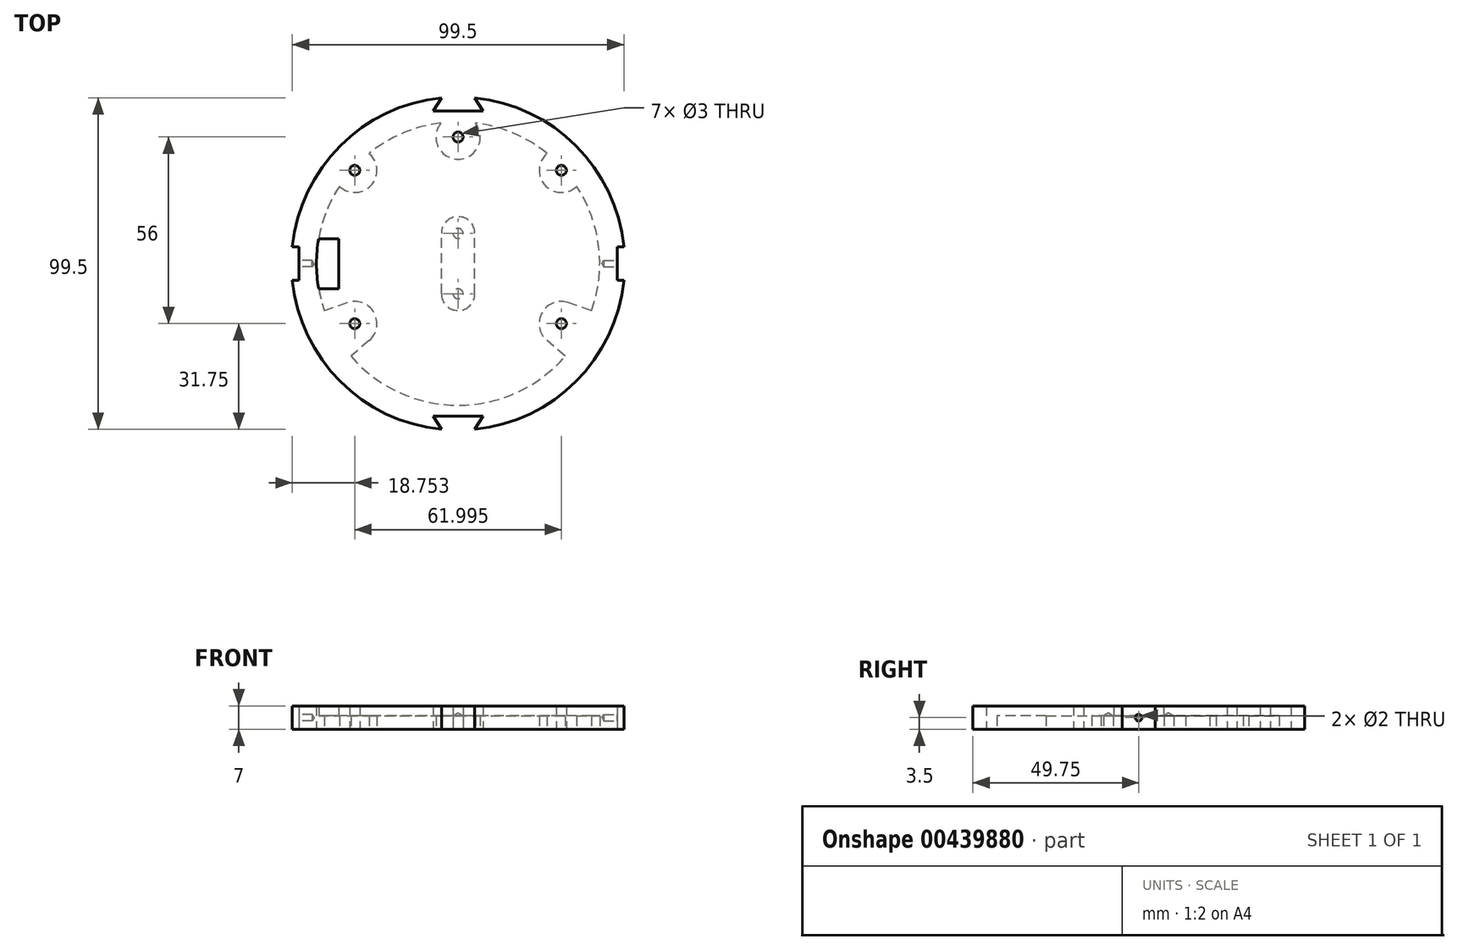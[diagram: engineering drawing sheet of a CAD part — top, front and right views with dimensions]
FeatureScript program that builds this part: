
annotation { "Feature Type Name" : "Feature", "Feature Type Description" : "" }
export const myFeature = defineFeature(function(context is Context, id is Id, definition is map)
    precondition{}
    {
        {
            var Q0;
            Q0=qCreatedBy(makeId("Top.planeOp"),FACE);
            var sketch = newSketch(context, id + "F0", { "sketchPlane" : qUnion([Q0])});
            skLineSegment(sketch, "E0", {"start": v(-49.75, 5) * mm, "end": v(-47.75, 5) * mm});
            skLineSegment(sketch, "E1.0.1.0", {"start": v(-49.75, -5) * mm, "end": v(-47.75, -5) * mm});
            skLineSegment(sketch, "E2.right", {"start": v(-47.75, 5) * mm, "end": v(-47.75, -5) * mm});
            skLineSegment(sketch, "E3.bottom", {"start": v(49.75, 5) * mm, "end": v(47.75, 5) * mm});
            skLineSegment(sketch, "E3.top", {"start": v(49.75, -5) * mm, "end": v(47.75, -5) * mm});
            skLineSegment(sketch, "E3.right", {"start": v(47.75, 5) * mm, "end": v(47.75, -5) * mm});
            skLineSegment(sketch, "E4.trimOffspring", {"start": v(47.75, 5) * mm, "end": v(49.75, 5) * mm});
            skLineSegment(sketch, "E5.trimOffspring", {"start": v(47.75, -5) * mm, "end": v(49.75, -5) * mm});
            skArc(sketch, "E6", {"start": v(-5, 49.75) * mm, "mid": v(-35.36, 35.36) * mm, "end": v(-49.75, 5) * mm});
            skArc(sketch, "E7.trimOffspring", {"start": v(-49.75, -5) * mm, "mid": v(-35.36, -35.36) * mm, "end": v(-5, -49.75) * mm});
            skArc(sketch, "E8.trimOffspring", {"start": v(49.75, 5) * mm, "mid": v(35.36, 35.36) * mm, "end": v(5, 49.75) * mm});
            skArc(sketch, "E9.trimOffspring", {"start": v(5, -49.75) * mm, "mid": v(35.36, -35.36) * mm, "end": v(49.75, -5) * mm});
            skCircle(sketch, "E10", {"center": v(-31, 28) * mm, "radius": 1.5 * mm});
            skCircle(sketch, "E11", {"center": v(0, 38) * mm, "radius": 1.5 * mm});
            skCircle(sketch, "E12", {"center": v(31, 28) * mm, "radius": 1.5 * mm});
            skCircle(sketch, "E13", {"center": v(-31, -18) * mm, "radius": 1.5 * mm});
            skCircle(sketch, "E14", {"center": v(31, -18) * mm, "radius": 1.5 * mm});
            skLineSegment(sketch, "E15", {"start": v(7.5, 45.75) * mm, "end": v(-7.5, 45.75) * mm});
            skLineSegment(sketch, "E16", {"start": v(-7.5, -45.75) * mm, "end": v(7.5, -45.75) * mm});
            skLineSegment(sketch, "E17", {"start": v(-5, 49.75) * mm, "end": v(-7.5, 45.75) * mm});
            skLineSegment(sketch, "E18", {"start": v(5, 49.75) * mm, "end": v(7.5, 45.75) * mm});
            skLineSegment(sketch, "E19", {"start": v(-7.5, -45.75) * mm, "end": v(-5, -49.75) * mm});
            skLineSegment(sketch, "E20", {"start": v(5, -49.75) * mm, "end": v(7.5, -45.75) * mm});
            skCircle(sketch, "E21", {"center": v(0, 0) * mm, "radius": 42.5 * mm, "construction": true});
            skLineSegment(sketch, "E22.bottom", {"start": v(-41.83, 7.5) * mm, "end": v(-35.83, 7.5) * mm});
            skLineSegment(sketch, "E22.top", {"start": v(-41.83, -7.5) * mm, "end": v(-35.83, -7.5) * mm});
            skLineSegment(sketch, "E22.left", {"start": v(-41.83, 7.5) * mm, "end": v(-41.83, -7.5) * mm});
            skLineSegment(sketch, "E22.right", {"start": v(-35.83, 7.5) * mm, "end": v(-35.83, -7.5) * mm});
            skArc(sketch, "E23", {"start": v(-41.83, 7.5) * mm, "mid": v(-42.5, 0) * mm, "end": v(-41.83, -7.5) * mm});
            skSolve(sketch);
        }
        {
            var Q0;
            Q0 = qSketchRegion(id + "F0", true);
            extrude(context, id + "F1", {"entities" : qUnion([Q0]), "offsetDistance" : 25 * mm, "depth" : 7 * mm});
        }
        {
            var Q0;
            Q0=makeQuery(id+"F1.opExtrude","CAP_FACE",FACE,{"disambiguationData":[OSD([sQuery(id+"F0.wireOp",EDGE,"E0"),sQuery(id+"F0.wireOp",EDGE,"E1.0.1.0"),sQuery(id+"F0.wireOp",EDGE,"E2.right"),sQuery(id+"F0.wireOp",EDGE,"E3.right"),sQuery(id+"F0.wireOp",EDGE,"6F78V14t-ZdTv-VjlB-1T6a-OLiU7aMDUZpK.top"),sQuery(id+"F0.wireOp",EDGE,"6F78V14t-ZdTv-VjlB-1T6a-OLiU7aMDUZpK.left"),sQuery(id+"F0.wireOp",EDGE,"6F78V14t-ZdTv-VjlB-1T6a-OLiU7aMDUZpK.right"),sQuery(id+"F0.wireOp",EDGE,"PvTYHQWE-3ALD-PmBr-tVXn-1hqZbBmZ8mVZ.top"),sQuery(id+"F0.wireOp",EDGE,"E4.trimOffspring"),sQuery(id+"F0.wireOp",EDGE,"E5.trimOffspring"),sQuery(id+"F0.wireOp",EDGE,"1bcc615c-06b4-494b-89bc-5a61939d49d9.trimOffspring"),sQuery(id+"F0.wireOp",EDGE,"d66e13da-aae6-4b5e-80dc-d0fbbee3e63b.trimOffspring"),sQuery(id+"F0.wireOp",EDGE,"E6"),sQuery(id+"F0.wireOp",EDGE,"E7.trimOffspring"),sQuery(id+"F0.wireOp",EDGE,"E8.trimOffspring"),sQuery(id+"F0.wireOp",EDGE,"E9.trimOffspring"),sQuery(id+"F0.wireOp",EDGE,"E10"),sQuery(id+"F0.wireOp",EDGE,"E11"),sQuery(id+"F0.wireOp",EDGE,"E12"),sQuery(id+"F0.wireOp",EDGE,"E13"),sQuery(id+"F0.wireOp",EDGE,"E14")])],"isStart":true});
            var sketch = newSketch(context, id + "F2", { "sketchPlane" : qUnion([Q0])});
            skArc(sketch, "E24", {"start": v(-40.08, 14.15) * mm, "mid": v(-42.2, -5.05) * mm, "end": v(-35.6, -23.2) * mm});
            skArc(sketch, "E25", {"start": v(-33.21, 11.72) * mm, "mid": v(-25.24, 14.66) * mm, "end": v(-26.64, 23.03) * mm});
            skArc(sketch, "E26", {"start": v(26.64, 23.03) * mm, "mid": v(25.24, 14.66) * mm, "end": v(33.21, 11.72) * mm});
            skArc(sketch, "E27", {"start": v(-26.7, -33.07) * mm, "mid": v(-26.06, -23.54) * mm, "end": v(-35.6, -23.2) * mm});
            skArc(sketch, "E28", {"start": v(35.6, -23.2) * mm, "mid": v(26.06, -23.54) * mm, "end": v(26.7, -33.07) * mm});
            skArc(sketch, "E29", {"start": v(5.18, -42.18) * mm, "mid": v(0, -31.34) * mm, "end": v(-5.18, -42.18) * mm});
            skLineSegment(sketch, "E30", {"start": v(-26.64, 23.03) * mm, "end": v(-32.15, 27.8) * mm});
            skLineSegment(sketch, "E31", {"start": v(-33.21, 11.72) * mm, "end": v(-40.08, 14.15) * mm});
            skLineSegment(sketch, "E32", {"start": v(32.15, 27.8) * mm, "end": v(26.64, 23.03) * mm});
            skLineSegment(sketch, "E33", {"start": v(40.08, 14.15) * mm, "end": v(33.21, 11.72) * mm});
            skArc(sketch, "E34.trimOffspring", {"start": v(32.15, 27.8) * mm, "mid": v(0, 42.5) * mm, "end": v(-32.15, 27.8) * mm});
            skArc(sketch, "E35.trimOffspring", {"start": v(-26.7, -33.07) * mm, "mid": v(-16.57, -39.14) * mm, "end": v(-5.18, -42.18) * mm});
            skArc(sketch, "E36.trimOffspring", {"start": v(35.6, -23.2) * mm, "mid": v(42.2, -5.05) * mm, "end": v(40.08, 14.15) * mm});
            skArc(sketch, "E37.trimOffspring", {"start": v(5.18, -42.18) * mm, "mid": v(16.57, -39.14) * mm, "end": v(26.7, -33.07) * mm});
            skSolve(sketch);
        }
        {
            var Q0;
            Q0 = qSketchRegion(id + "F2", true);
            extrude(context, id + "F3", {"entities" : qUnion([Q0]), "operationType" : NewBodyOperationType.REMOVE, "oppositeDirection" : true, "depth" : 4 * mm});
        }
        {
            var Q0;
            Q0=makeQuery(id+"F1.opExtrude","SWEPT_FACE",FACE,{"disambiguationData":[OSD([sQuery(id+"F0.wireOp",EDGE,"E2.right")])]});
            var sketch = newSketch(context, id + "F4", { "sketchPlane" : qUnion([Q0])});
            skCircle(sketch, "E38", {"center": v(0, 3.5) * mm, "radius": 1.5 * mm});
            skSolve(sketch);
        }
        {
            var Q0;
            Q0=sQuery(id+"F4.wireOp",VERTEX,"E38.center");
            var Q1;
            Q1=makeQuery(id+"F1.opExtrude","SWEPT_BODY",BODY,{"disambiguationData":[OSD([sQuery(id+"F0.wireOp",EDGE,"E0"),sQuery(id+"F0.wireOp",EDGE,"E1.0.1.0"),sQuery(id+"F0.wireOp",EDGE,"E2.right"),sQuery(id+"F0.wireOp",EDGE,"E3.right"),sQuery(id+"F0.wireOp",EDGE,"6F78V14t-ZdTv-VjlB-1T6a-OLiU7aMDUZpK.top"),sQuery(id+"F0.wireOp",EDGE,"6F78V14t-ZdTv-VjlB-1T6a-OLiU7aMDUZpK.left"),sQuery(id+"F0.wireOp",EDGE,"6F78V14t-ZdTv-VjlB-1T6a-OLiU7aMDUZpK.right"),sQuery(id+"F0.wireOp",EDGE,"PvTYHQWE-3ALD-PmBr-tVXn-1hqZbBmZ8mVZ.top"),sQuery(id+"F0.wireOp",EDGE,"E4.trimOffspring"),sQuery(id+"F0.wireOp",EDGE,"E5.trimOffspring"),sQuery(id+"F0.wireOp",EDGE,"1bcc615c-06b4-494b-89bc-5a61939d49d9.trimOffspring"),sQuery(id+"F0.wireOp",EDGE,"d66e13da-aae6-4b5e-80dc-d0fbbee3e63b.trimOffspring"),sQuery(id+"F0.wireOp",EDGE,"E6"),sQuery(id+"F0.wireOp",EDGE,"E7.trimOffspring"),sQuery(id+"F0.wireOp",EDGE,"E8.trimOffspring"),sQuery(id+"F0.wireOp",EDGE,"E9.trimOffspring"),sQuery(id+"F0.wireOp",EDGE,"E10"),sQuery(id+"F0.wireOp",EDGE,"E11"),sQuery(id+"F0.wireOp",EDGE,"E12"),sQuery(id+"F0.wireOp",EDGE,"E13"),sQuery(id+"F0.wireOp",EDGE,"E14")])]});
            hole(context, id + "F5", {"style" : HoleStyle.SIMPLE, "endStyle" : HoleEndStyle.BLIND, "holeDiameter" : 2 * mm, "holeDepth" : 4 * mm, "isTappedThrough" : true, "tappedDepth" : 12 * mm, "tapClearance" : 3, "startFromSketch" : true, "locations" : qUnion([Q0]), "scope" : qUnion([Q1])});
        }
        {
            var Q0;
            Q0=makeQuery(id+"F1.opExtrude","SWEPT_FACE",FACE,{"disambiguationData":[OSD([sQuery(id+"F0.wireOp",EDGE,"E3.right")])]});
            var sketch = newSketch(context, id + "F6", { "sketchPlane" : qUnion([Q0])});
            skCircle(sketch, "E39", {"center": v(0, 3.5) * mm, "radius": 0.95 * mm});
            skSolve(sketch);
        }
        {
            var Q0;
            Q0=sQuery(id+"F6.wireOp",VERTEX,"E39.center");
            var Q1;
            Q1=makeQuery(id+"F1.opExtrude","SWEPT_BODY",BODY,{"disambiguationData":[OSD([sQuery(id+"F0.wireOp",EDGE,"E0"),sQuery(id+"F0.wireOp",EDGE,"E1.0.1.0"),sQuery(id+"F0.wireOp",EDGE,"E2.right"),sQuery(id+"F0.wireOp",EDGE,"E3.right"),sQuery(id+"F0.wireOp",EDGE,"6F78V14t-ZdTv-VjlB-1T6a-OLiU7aMDUZpK.top"),sQuery(id+"F0.wireOp",EDGE,"6F78V14t-ZdTv-VjlB-1T6a-OLiU7aMDUZpK.left"),sQuery(id+"F0.wireOp",EDGE,"6F78V14t-ZdTv-VjlB-1T6a-OLiU7aMDUZpK.right"),sQuery(id+"F0.wireOp",EDGE,"PvTYHQWE-3ALD-PmBr-tVXn-1hqZbBmZ8mVZ.top"),sQuery(id+"F0.wireOp",EDGE,"E4.trimOffspring"),sQuery(id+"F0.wireOp",EDGE,"E5.trimOffspring"),sQuery(id+"F0.wireOp",EDGE,"1bcc615c-06b4-494b-89bc-5a61939d49d9.trimOffspring"),sQuery(id+"F0.wireOp",EDGE,"d66e13da-aae6-4b5e-80dc-d0fbbee3e63b.trimOffspring"),sQuery(id+"F0.wireOp",EDGE,"E6"),sQuery(id+"F0.wireOp",EDGE,"E7.trimOffspring"),sQuery(id+"F0.wireOp",EDGE,"E8.trimOffspring"),sQuery(id+"F0.wireOp",EDGE,"E9.trimOffspring"),sQuery(id+"F0.wireOp",EDGE,"E10"),sQuery(id+"F0.wireOp",EDGE,"E11"),sQuery(id+"F0.wireOp",EDGE,"E12"),sQuery(id+"F0.wireOp",EDGE,"E13"),sQuery(id+"F0.wireOp",EDGE,"E14")])]});
            hole(context, id + "F7", {"style" : HoleStyle.SIMPLE, "endStyle" : HoleEndStyle.BLIND, "holeDiameter" : 2 * mm, "holeDepth" : 4 * mm, "isTappedThrough" : true, "tappedDepth" : 12 * mm, "tapClearance" : 3, "startFromSketch" : true, "locations" : qUnion([Q0]), "scope" : qUnion([Q1])});
        }
        {
            var Q0;
            Q0=qCreatedBy(makeId("Top.planeOp"),FACE);
            var sketch = newSketch(context, id + "F8", { "sketchPlane" : qUnion([Q0])});
            skArc(sketch, "E40", {"start": v(-4.99, -9.06) * mm, "mid": v(0.01, -14.06) * mm, "end": v(5.01, -9.06) * mm});
            skArc(sketch, "E41", {"start": v(5.01, 9.07) * mm, "mid": v(0.01, 14.07) * mm, "end": v(-4.99, 9.07) * mm});
            skLineSegment(sketch, "E42", {"start": v(5.01, -9.06) * mm, "end": v(5.01, 9.07) * mm});
            skLineSegment(sketch, "E43", {"start": v(-4.99, -9.06) * mm, "end": v(-4.99, 9.07) * mm});
            skSolve(sketch);
        }
        {
            var Q0;
            Q0=makeQuery(id+"F8.imprint","IMPRINT",FACE,{"disambiguationData":[TD([[makeQuery(id+"F8.imprint","IMPRINT",EDGE,{"derivedFrom":sQuery(id+"F8.wireOp",EDGE,"E40")}),1.0]])]});
            extrude(context, id + "F9", {"entities" : qUnion([Q0]), "operationType" : NewBodyOperationType.ADD, "depth" : 4 * mm});
        }
        {
            var Q0;
            Q0=sQuery(id+"F8.wireOp",VERTEX,"E40.center");
            var Q1;
            Q1=sQuery(id+"F8.wireOp",VERTEX,"E41.center");
            var Q2;
            Q2=makeQuery(id+"F1.opExtrude","SWEPT_BODY",BODY,{"disambiguationData":[OSD([sQuery(id+"F0.wireOp",EDGE,"E0"),sQuery(id+"F0.wireOp",EDGE,"E1.0.1.0"),sQuery(id+"F0.wireOp",EDGE,"E2.right"),sQuery(id+"F0.wireOp",EDGE,"E3.right"),sQuery(id+"F0.wireOp",EDGE,"E4.trimOffspring"),sQuery(id+"F0.wireOp",EDGE,"E5.trimOffspring"),sQuery(id+"F0.wireOp",EDGE,"E6"),sQuery(id+"F0.wireOp",EDGE,"E7.trimOffspring"),sQuery(id+"F0.wireOp",EDGE,"E8.trimOffspring"),sQuery(id+"F0.wireOp",EDGE,"E9.trimOffspring"),sQuery(id+"F0.wireOp",EDGE,"E10"),sQuery(id+"F0.wireOp",EDGE,"E11"),sQuery(id+"F0.wireOp",EDGE,"E12"),sQuery(id+"F0.wireOp",EDGE,"E13"),sQuery(id+"F0.wireOp",EDGE,"E14"),sQuery(id+"F0.wireOp",EDGE,"E15"),sQuery(id+"F0.wireOp",EDGE,"E16"),sQuery(id+"F0.wireOp",EDGE,"E17"),sQuery(id+"F0.wireOp",EDGE,"E18"),sQuery(id+"F0.wireOp",EDGE,"E19"),sQuery(id+"F0.wireOp",EDGE,"E20")])]});
            hole(context, id + "F10", {"style" : HoleStyle.SIMPLE, "endStyle" : HoleEndStyle.BLIND, "oppositeDirection" : true, "holeDiameter" : 3 * mm, "holeDepth" : 4 * mm, "isTappedThrough" : true, "tappedDepth" : 12 * mm, "tapClearance" : 3, "startFromSketch" : true, "locations" : qUnion([Q0, Q1]), "scope" : qUnion([Q2])});
        }
    });
